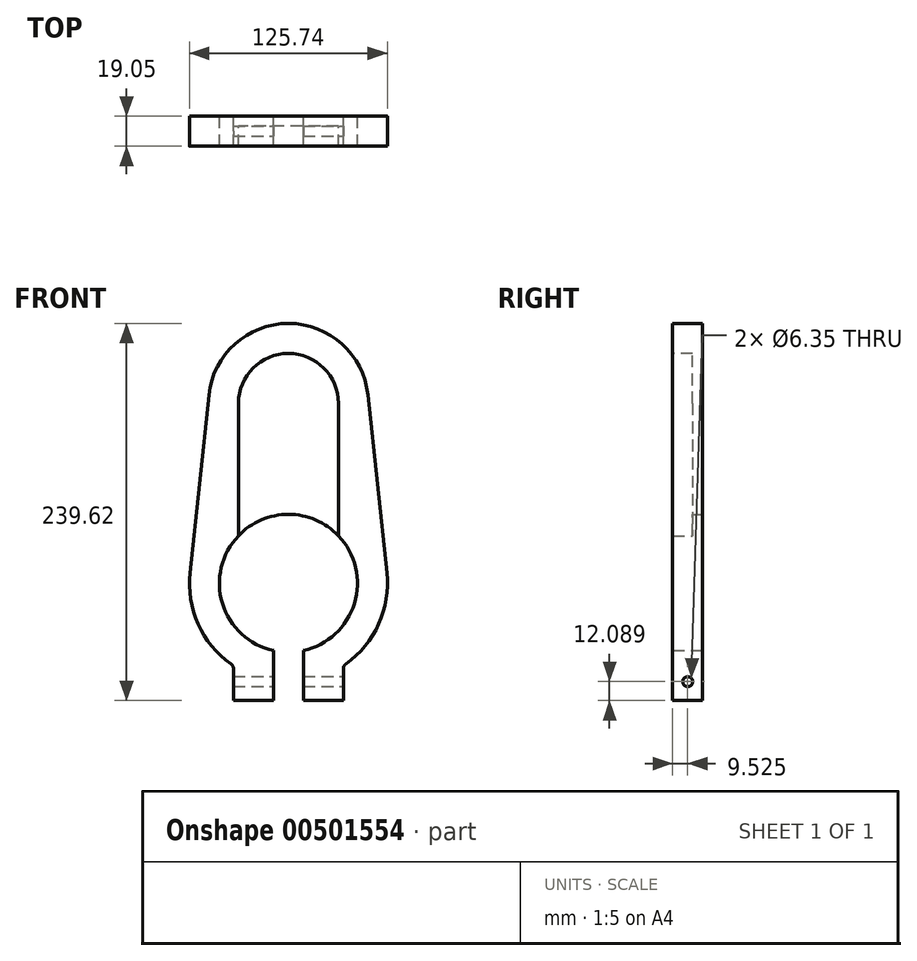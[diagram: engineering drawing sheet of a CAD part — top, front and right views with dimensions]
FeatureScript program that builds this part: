
annotation { "Feature Type Name" : "Feature", "Feature Type Description" : "" }
export const myFeature = defineFeature(function(context is Context, id is Id, definition is map)
    precondition{}
    {
        {
            var Q0;
            Q0=qCreatedBy(makeId("Front.planeOp"),FACE);
            var sketch = newSketch(context, id + "F0", { "sketchPlane" : qUnion([Q0])});
            skArc(sketch, "E0", {"start": v(9.53, -42.77) * mm, "mid": v(0, 43.82) * mm, "end": v(-9.53, -42.77) * mm});
            skArc(sketch, "E1", {"start": v(34.93, -52.27) * mm, "mid": v(56.93, -26.66) * mm, "end": v(62.51, 6.64) * mm});
            skLineSegment(sketch, "E2", {"start": v(-62.51, 6.64) * mm, "end": v(-50.52, 119.66) * mm});
            skLineSegment(sketch, "E3", {"start": v(62.51, 6.64) * mm, "end": v(50.52, 119.66) * mm});
            skCircle(sketch, "E4", {"center": v(0, 114.3) * mm, "radius": 31.75 * mm, "construction": true});
            skLineSegment(sketch, "E5", {"start": v(0, 0) * mm, "end": v(0, 114.3) * mm, "construction": true});
            skArc(sketch, "E6", {"start": v(50.52, 119.66) * mm, "mid": v(0, 165.1) * mm, "end": v(-50.52, 119.66) * mm});
            skLineSegment(sketch, "E7", {"start": v(-9.52, -42.77) * mm, "end": v(-9.52, -74.52) * mm});
            skLineSegment(sketch, "E8", {"start": v(-9.52, -74.52) * mm, "end": v(-34.93, -74.52) * mm});
            skLineSegment(sketch, "E9", {"start": v(-34.93, -74.52) * mm, "end": v(-34.93, -52.27) * mm});
            skLineSegment(sketch, "E10.MirrorCS", {"start": v(9.52, -42.77) * mm, "end": v(9.52, -74.52) * mm});
            skLineSegment(sketch, "E11.MirrorCS", {"start": v(34.93, -74.52) * mm, "end": v(34.93, -52.27) * mm});
            skLineSegment(sketch, "E12.MirrorCS", {"start": v(9.52, -74.52) * mm, "end": v(34.93, -74.52) * mm});
            skArc(sketch, "E13.trimOffspring", {"start": v(-62.51, 6.64) * mm, "mid": v(-56.93, -26.66) * mm, "end": v(-34.93, -52.27) * mm});
            skSolve(sketch);
        }
        {
            var Q0;
            Q0=makeQuery(id+"F0.imprint","IMPRINT",FACE,{"disambiguationData":[TD([[makeQuery(id+"F0.imprint","IMPRINT",EDGE,{"derivedFrom":sQuery(id+"F0.wireOp",EDGE,"E0")}),-1.0]])]});
            extrude(context, id + "F1", {"entities" : qUnion([Q0]), "depth" : 19.05 * mm});
        }
        {
            var Q0;
            Q0=makeQuery(id+"F1.opExtrude","CAP_FACE",FACE,{"disambiguationData":[OSD([sQuery(id+"F0.wireOp",EDGE,"E0"),sQuery(id+"F0.wireOp",EDGE,"E1"),sQuery(id+"F0.wireOp",EDGE,"E2"),sQuery(id+"F0.wireOp",EDGE,"E3"),sQuery(id+"F0.wireOp",EDGE,"E6"),sQuery(id+"F0.wireOp",EDGE,"E7"),sQuery(id+"F0.wireOp",EDGE,"E8"),sQuery(id+"F0.wireOp",EDGE,"E9"),sQuery(id+"F0.wireOp",EDGE,"E10.MirrorCS"),sQuery(id+"F0.wireOp",EDGE,"E11.MirrorCS"),sQuery(id+"F0.wireOp",EDGE,"E12.MirrorCS"),sQuery(id+"F0.wireOp",EDGE,"E13.trimOffspring")])],"isStart":false});
            var sketch = newSketch(context, id + "F2", { "sketchPlane" : qUnion([Q0])});
            skArc(sketch, "E14", {"start": v(31.75, 114.3) * mm, "mid": v(0, 146.05) * mm, "end": v(-31.75, 114.3) * mm});
            skLineSegment(sketch, "E15", {"start": v(-31.75, 114.3) * mm, "end": v(-31.75, 12.7) * mm});
            skLineSegment(sketch, "E16", {"start": v(31.75, 114.3) * mm, "end": v(31.75, 12.7) * mm});
            skLineSegment(sketch, "E17", {"start": v(31.75, 12.7) * mm, "end": v(-31.75, 12.7) * mm});
            skSolve(sketch);
        }
        {
            var Q0;
            Q0 = qSketchRegion(id + "F2", true);
            extrude(context, id + "F3", {"entities" : qUnion([Q0]), "operationType" : NewBodyOperationType.REMOVE, "oppositeDirection" : true, "depth" : 12.7 * mm});
        }
        {
            var Q0;
            Q0=makeQuery(id+"F1.opExtrude","SWEPT_FACE",FACE,{"disambiguationData":[OSD([sQuery(id+"F0.wireOp",EDGE,"E11.MirrorCS")])]});
            var sketch = newSketch(context, id + "F4", { "sketchPlane" : qUnion([Q0])});
            skPoint(sketch, "E18", {"position": v(-9.53, -62.43) * mm});
            skPoint(sketch, "E18.positionSnap0", {"position": v(-9.53, -52.27) * mm});
            skSolve(sketch);
        }
        {
            var Q0;
            Q0=sQuery(id+"F4.wireOp",VERTEX,"E18");
            var Q1;
            Q1=makeQuery(id+"F1.opExtrude","SWEPT_BODY",BODY,{"disambiguationData":[OSD([sQuery(id+"F0.wireOp",EDGE,"E0"),sQuery(id+"F0.wireOp",EDGE,"E1"),sQuery(id+"F0.wireOp",EDGE,"E2"),sQuery(id+"F0.wireOp",EDGE,"E3"),sQuery(id+"F0.wireOp",EDGE,"E6"),sQuery(id+"F0.wireOp",EDGE,"E7"),sQuery(id+"F0.wireOp",EDGE,"E8"),sQuery(id+"F0.wireOp",EDGE,"E9"),sQuery(id+"F0.wireOp",EDGE,"E10.MirrorCS"),sQuery(id+"F0.wireOp",EDGE,"E11.MirrorCS"),sQuery(id+"F0.wireOp",EDGE,"E12.MirrorCS"),sQuery(id+"F0.wireOp",EDGE,"E13.trimOffspring")])]});
            hole(context, id + "F5", {"style" : HoleStyle.SIMPLE, "endStyle" : HoleEndStyle.THROUGH, "holeDiameter" : 6.35 * mm, "isTappedThrough" : true, "tappedDepth" : 12.7 * mm, "tapClearance" : 3, "locations" : qUnion([Q0]), "scope" : qUnion([Q1])});
        }
        {
            var Q0;
            Q0=makeQuery(id+"F1.opExtrude","SWEPT_EDGE",EDGE,{"disambiguationData":[OSD([sQuery(id+"F0.wireOp",EDGE,"E1"),sQuery(id+"F0.wireOp",EDGE,"E11.MirrorCS")])]});
            var Q1;
            Q1=makeQuery(id+"F1.opExtrude","SWEPT_EDGE",EDGE,{"disambiguationData":[OSD([sQuery(id+"F0.wireOp",EDGE,"E9"),sQuery(id+"F0.wireOp",EDGE,"E13.trimOffspring")])]});
            fillet(context, id + "F6", {"entities" : qUnion([Q0, Q1]), "radius" : 3.8 * mm, "tangentPropagation" : true, "allowEdgeOverflow" : false});
        }
    });
